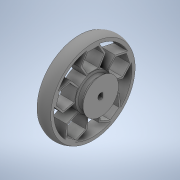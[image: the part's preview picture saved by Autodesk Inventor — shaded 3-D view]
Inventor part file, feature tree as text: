
AUTODESK INVENTOR PART (.ipt)
format: ipt  version: 2020 (Build 240168000, 168)  size: 428,032 bytes
history: native  units: in
note: dims shown in document units (in); Inventor stores cm internally (conversion verified against a paired STEP export)
features: sketch x4, extrude x2, revolve x2, projected_geometry x1
ambient origin geometry x8: Origin, YZ Plane, XZ Plane, XY Plane, X Axis, Y Axis, Z Axis, Center Point
bodies: Solid1 (feature_tree)
feature tree (9):
  extrude  "Extrusion1"  Depth=0.0394in
  sketch  "Sketch3"  dims[d6=0.7087in d7=0.1575in]
  revolve  "Revolution1"  [1 undecoded]
  extrude  "Extrusion2"  Depth=0.1575in
  revolve  "Revolution2"  [1 undecoded]
  sketch  "Sketch1"  dims[d0=0.1181in d1=0.0394in]
  sketch  "Sketch2"  dims[d3=1.6929in d4=0.1181in]
  projected_geometry  "Projected Loop1"
  sketch  "Sketch4"  dims[d8=0.0in d9=1.6929in d10=0.063in d11=0.0315in d16=0.2756in d17=0.0in d19=360.0deg d20=0.0787in d24=0.0394in d25=90.0deg d26=45.0deg d28=0.0079in d29=1.9685in d31=360.0deg]
note: 2 required parameter values undecoded (feature->parameter linkage not recoverable at this tier; creation-order binding heuristic only, values carry confidence <= 0.55)
